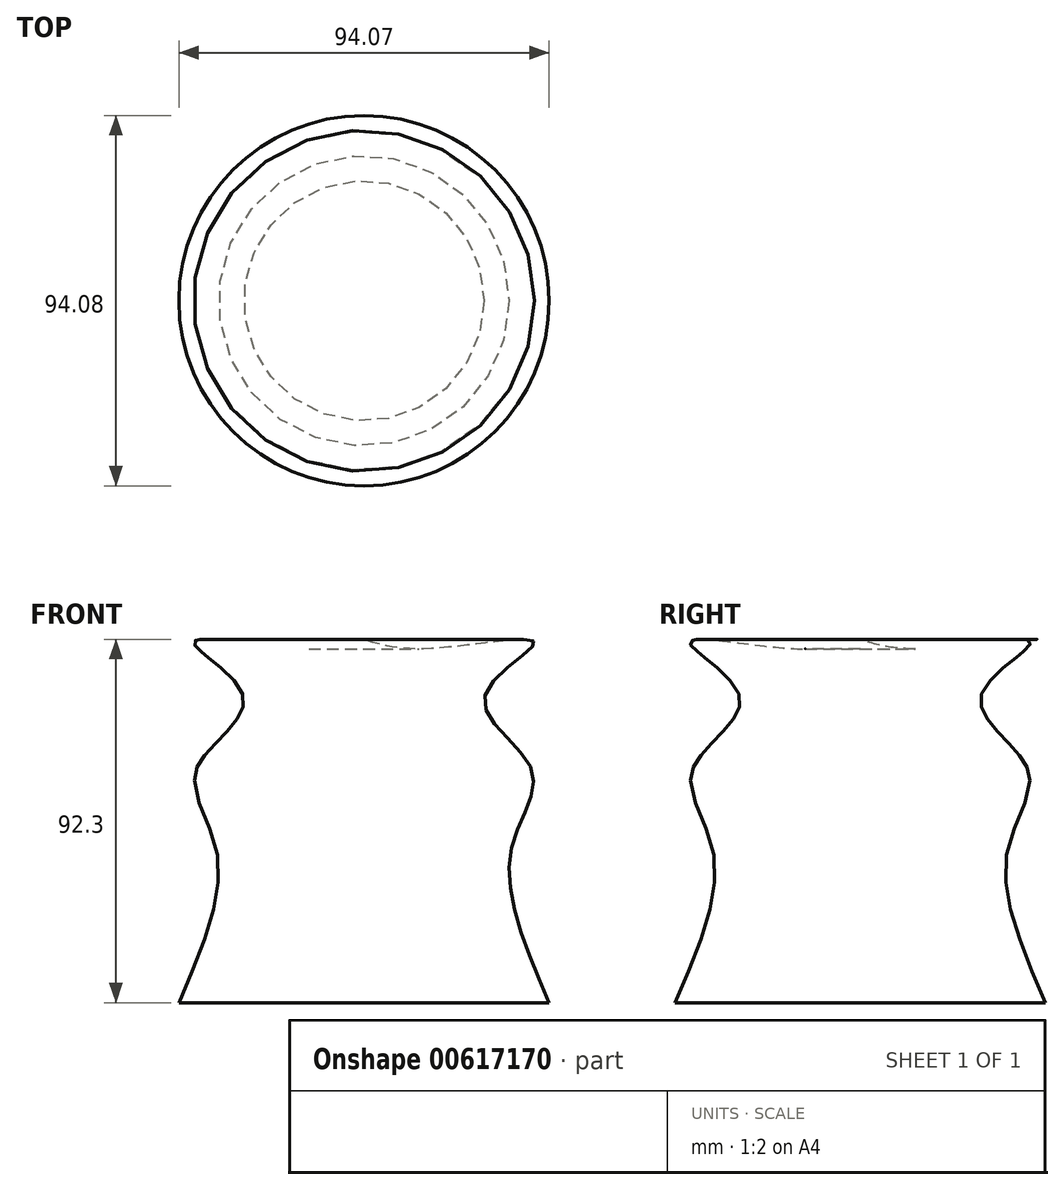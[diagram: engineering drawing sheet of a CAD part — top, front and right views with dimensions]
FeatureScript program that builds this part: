
annotation { "Feature Type Name" : "Feature", "Feature Type Description" : "" }
export const myFeature = defineFeature(function(context is Context, id is Id, definition is map)
    precondition{}
    {
        {
            var Q0;
            Q0=qCreatedBy(makeId("Front.planeOp"),FACE);
            var sketch = newSketch(context, id + "F0", { "sketchPlane" : qUnion([Q0])});
            skLineSegment(sketch, "E0", {"start": v(-20.35, 41.62) * mm, "end": v(-20.35, -50.58) * mm});
            skLineSegment(sketch, "E1", {"start": v(-20.35, -50.58) * mm, "end": v(26.7, -50.58) * mm});
            skFitSpline(sketch, "E2", {"points": [v(26.7, -50.58) * mm, v(16.99, -12.13) * mm, v(22.21, 8.77) * mm, v(10.27, 27.06) * mm, v(22.96, 40.88) * mm, v(-3.17, 39.38) * mm, v(-20.35, 41.62) * mm], "startDerivative": vector(-82.58, 191.18) * mm, "endDerivative": vector(-93.63, 28.42) * mm});
            skSolve(sketch);
        }
        {
            var Q0;
            Q0 = qSketchRegion(id + "F0", true);
            var Q1;
            Q1=sQuery(id+"F0.wireOp",EDGE,"E0");
            revolve(context, id + "F1", {"entities" : qUnion([Q0]), "axis" : qUnion([Q1]), "revolveType" : RevolveType.FULL});
        }
    });
